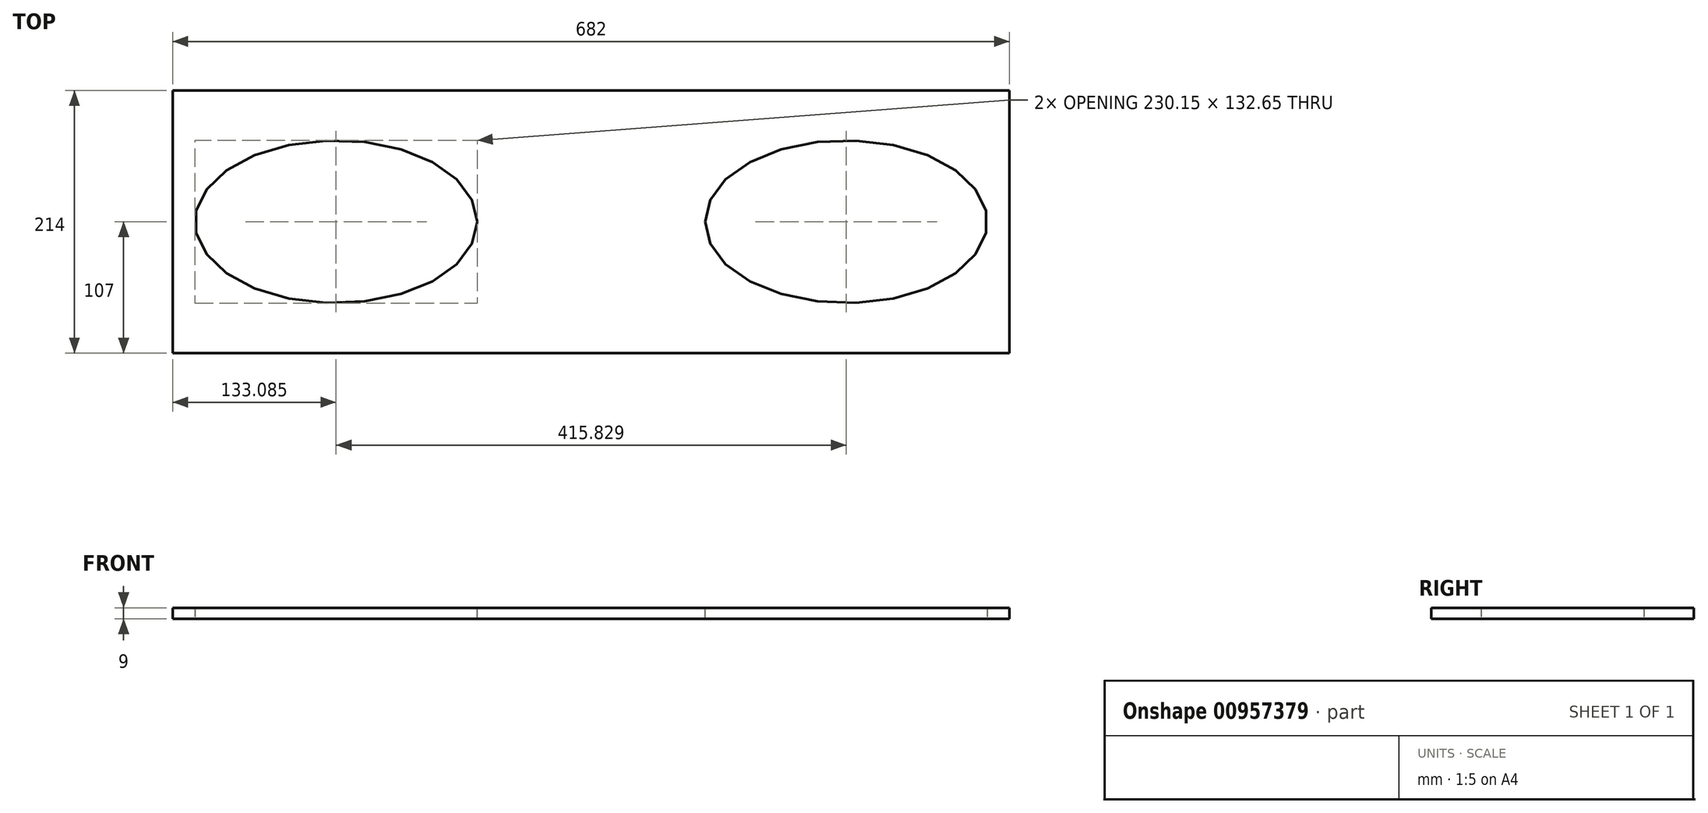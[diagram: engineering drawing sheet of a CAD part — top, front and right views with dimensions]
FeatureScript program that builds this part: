
annotation { "Feature Type Name" : "Feature", "Feature Type Description" : "" }
export const myFeature = defineFeature(function(context is Context, id is Id, definition is map)
    precondition{}
    {
        {
            var Q0;
            Q0=qCreatedBy(makeId("Top.planeOp"),FACE);
            var sketch = newSketch(context, id + "F0", { "sketchPlane" : qUnion([Q0])});
            skLineSegment(sketch, "E0.bottom", {"start": v(341, 107) * mm, "end": v(-341, 107) * mm});
            skLineSegment(sketch, "E0.top", {"start": v(341, -107) * mm, "end": v(-341, -107) * mm});
            skLineSegment(sketch, "E0.left", {"start": v(341, 107) * mm, "end": v(341, -107) * mm});
            skLineSegment(sketch, "E0.right", {"start": v(-341, 107) * mm, "end": v(-341, -107) * mm});
            skPoint(sketch, "E0.middle", {"position": v(0, 0) * mm});
            skSolve(sketch);
        }
        {
            var Q0;
            Q0=makeQuery(id+"F0.imprint","IMPRINT",FACE,{"disambiguationData":[TD([[makeQuery(id+"F0.imprint","IMPRINT",EDGE,{"derivedFrom":sQuery(id+"F0.wireOp",EDGE,"E0.bottom")}),1.0]])]});
            extrude(context, id + "F1", {"entities" : qUnion([Q0]), "depth" : 9 * mm, "offsetDistance" : 25 * mm});
        }
        {
            var Q0;
            Q0=makeQuery(id+"F1.opExtrude","CAP_FACE",FACE,{"disambiguationData":[OSD([sQuery(id+"F0.wireOp",EDGE,"E0.bottom"),sQuery(id+"F0.wireOp",EDGE,"E0.top"),sQuery(id+"F0.wireOp",EDGE,"E0.left"),sQuery(id+"F0.wireOp",EDGE,"E0.right")])],"isStart":false});
            var sketch = newSketch(context, id + "F2", { "sketchPlane" : qUnion([Q0])});
            skEllipse(sketch, "E1", {"center": v(-207.91, 0) * mm, "majorRadius": 115.07 * mm, "minorRadius": 66.32 * mm, "majorAxis": v(1, 0)});
            skLineSegment(sketch, "E2", {"start": v(0, 0) * mm, "end": v(0, 49.69) * mm});
            skEllipse(sketch, "E3.MirrorC", {"center": v(207.91, 0) * mm, "majorRadius": 115.07 * mm, "minorRadius": 66.32 * mm, "majorAxis": v(-1, 0)});
            skSolve(sketch);
        }
        {
            var Q0;
            Q0=qSketchRegion(id+"F2",true);
            extrude(context, id + "F3", {"entities" : qUnion([Q0]), "operationType" : NewBodyOperationType.REMOVE, "oppositeDirection" : true, "depth" : 25 * mm, "offsetDistance" : 25 * mm});
        }
    });
